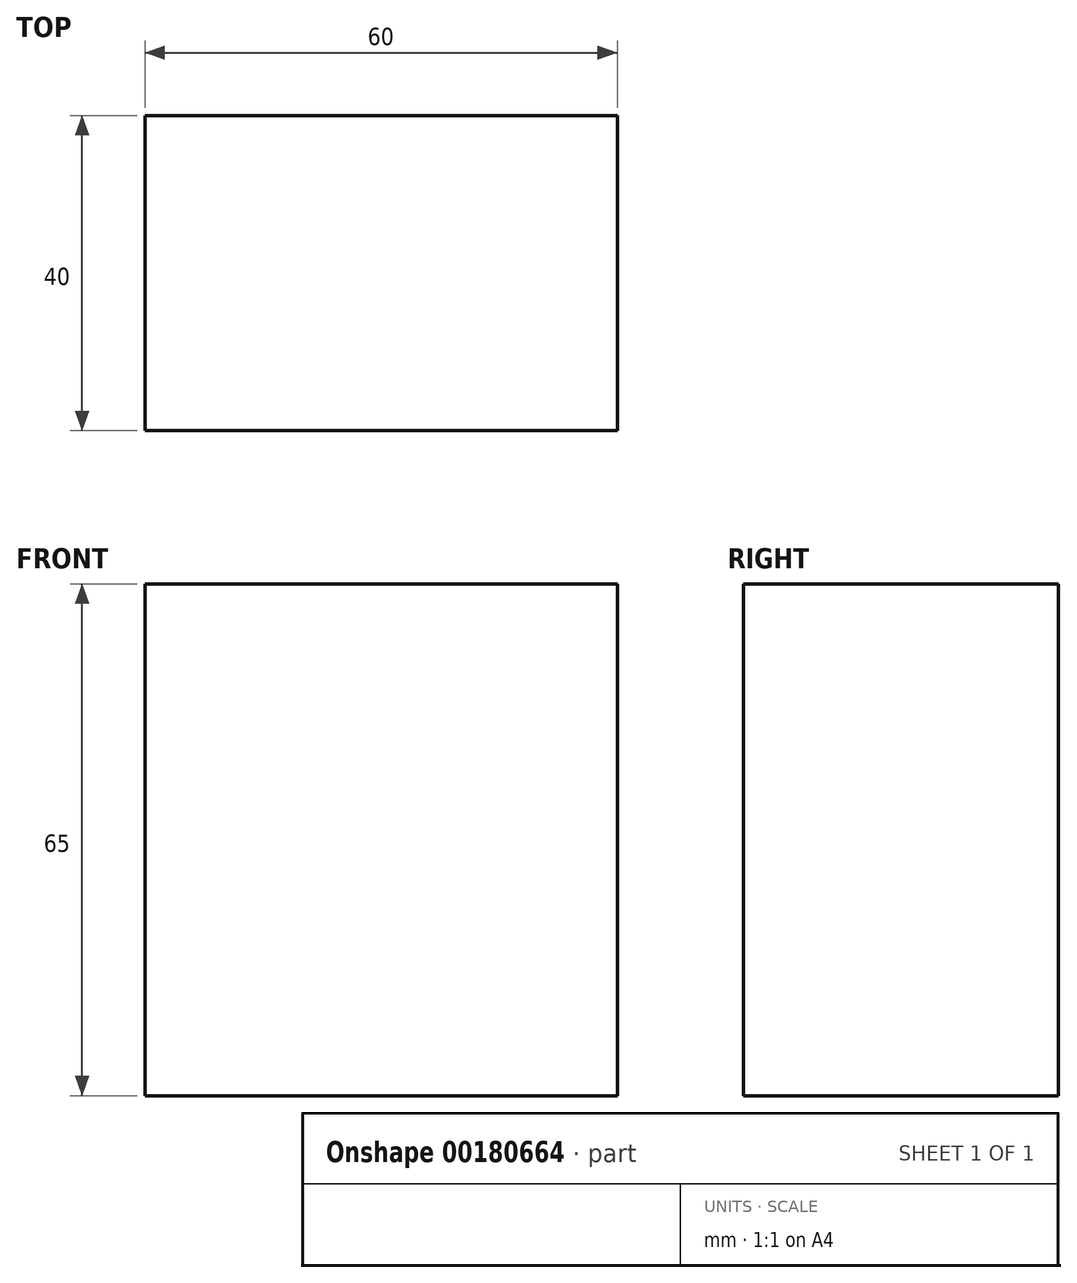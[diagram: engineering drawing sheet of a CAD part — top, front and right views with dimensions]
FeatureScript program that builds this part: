
annotation { "Feature Type Name" : "Feature", "Feature Type Description" : "" }
export const myFeature = defineFeature(function(context is Context, id is Id, definition is map)
    precondition{}
    {
        {
            var Q0;
            Q0=qCreatedBy(makeId("Top.planeOp"),FACE);
            var sketch = newSketch(context, id + "F0", { "sketchPlane" : qUnion([Q0])});
            skLineSegment(sketch, "E0.bottom", {"start": v(0, 0) * mm, "end": v(60, 0) * mm});
            skLineSegment(sketch, "E0.top", {"start": v(0, -40) * mm, "end": v(60, -40) * mm});
            skLineSegment(sketch, "E0.left", {"start": v(0, 0) * mm, "end": v(0, -40) * mm});
            skLineSegment(sketch, "E0.right", {"start": v(60, 0) * mm, "end": v(60, -40) * mm});
            skSolve(sketch);
        }
        {
            var Q0;
            Q0 = qSketchRegion(id + "F0", true);
            extrude(context, id + "F1", {"entities" : qUnion([Q0]), "depth" : 40 * mm});
        }
        {
            var Q0;
            Q0=makeQuery(id+"F1.opExtrude","CAP_FACE",FACE,{"disambiguationData":[OSD([sQuery(id+"F0.wireOp",EDGE,"E0.bottom"),sQuery(id+"F0.wireOp",EDGE,"E0.top"),sQuery(id+"F0.wireOp",EDGE,"E0.left"),sQuery(id+"F0.wireOp",EDGE,"E0.right")])],"isStart":false});
            var sketch = newSketch(context, id + "F2", { "sketchPlane" : qUnion([Q0])});
            skLineSegment(sketch, "E1", {"start": v(0, 0) * mm, "end": v(60, -40) * mm, "construction": true});
            skLineSegment(sketch, "E2", {"start": v(0, -40) * mm, "end": v(60, 0) * mm, "construction": true});
            skCircle(sketch, "E3", {"center": v(30, -20) * mm, "radius": 20 * mm});
            skSolve(sketch);
        }
        {
            var Q0;
            Q0=sQuery(id+"F2.wireOp",EDGE,"E3");
            var Q1;
            Q1=makeQuery(id+"F1.opExtrude","CAP_EDGE",EDGE,{"disambiguationData":[OSD([sQuery(id+"F0.wireOp",EDGE,"E0.left")])],"isStart":false});
            revolve(context, id + "F3", {"bodyType" : ToolBodyType.SURFACE, "surfaceEntities" : qUnion([Q0]), "axis" : qUnion([Q1]), "revolveType" : RevolveType.ONE_DIRECTION, "angle" : 270 * degree});
        }
        {
            var Q0;
            Q0=makeQuery(id+"F1.opExtrude","CAP_FACE",FACE,{"disambiguationData":[OSD([sQuery(id+"F0.wireOp",EDGE,"E0.bottom"),sQuery(id+"F0.wireOp",EDGE,"E0.top"),sQuery(id+"F0.wireOp",EDGE,"E0.left"),sQuery(id+"F0.wireOp",EDGE,"E0.right")])],"isStart":true});
            extrude(context, id + "F4", {"entities" : qUnion([Q0]), "operationType" : NewBodyOperationType.ADD, "depth" : 25 * mm});
        }
    });
